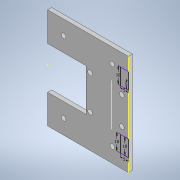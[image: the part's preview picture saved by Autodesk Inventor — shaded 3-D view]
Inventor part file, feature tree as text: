
AUTODESK INVENTOR PART (.ipt)
format: ipt  version: 2021 (Build 250183000, 183)  size: 148,480 bytes
history: native  units: in
note: dims shown in document units (in); Inventor stores cm internally (conversion verified against a paired STEP export)
features: reference x18, other x5, extrude x2, sketch x2
ambient origin geometry x8: Origin, YZ Plane, XZ Plane, XY Plane, X Axis, Y Axis, Z Axis, Center Point
bodies: Solid1 (feature_tree)
feature tree (27):
  extrude  "Extrusion1"  Depth=0.1142in
  extrude  "Extrusion3"  Depth=0.0984in TaperAngle=0.0deg
  sketch  "Sketch1"  dims[d0=0.1142in d1=0.1142in]
  reference  "Reference1"
  reference  "Reference2"
  reference  "Reference3"
  reference  "Reference4"
  reference  "Reference5"
  reference  "Reference6"
  reference  "Reference7"
  reference  "Reference8"
  reference  "Reference9"
  reference  "Reference10"
  reference  "Reference11"
  reference  "Reference12"
  reference  "Reference15"
  reference  "Reference16"
  reference  "Reference17"
  reference  "Reference18"
  reference  "Reference19"
  reference  "Reference20"
  sketch  "Sketch4"  dims[d2=0.2362in d15=0.0984in d16=0.0in d29=0.0591in d30=0.0in]
  parser-record x1  (decoder bookkeeping rows leaked as tree rows — omitted from the tree; the rows remain in map.json)
  other  "assembly.iam"
  other  "DIN_mount:12"
  other  "DIN_mount:11"
  other  "MPU-9255:1"
note: 1 file-system path scrubbed to <path> (originals preserved in map.json)
